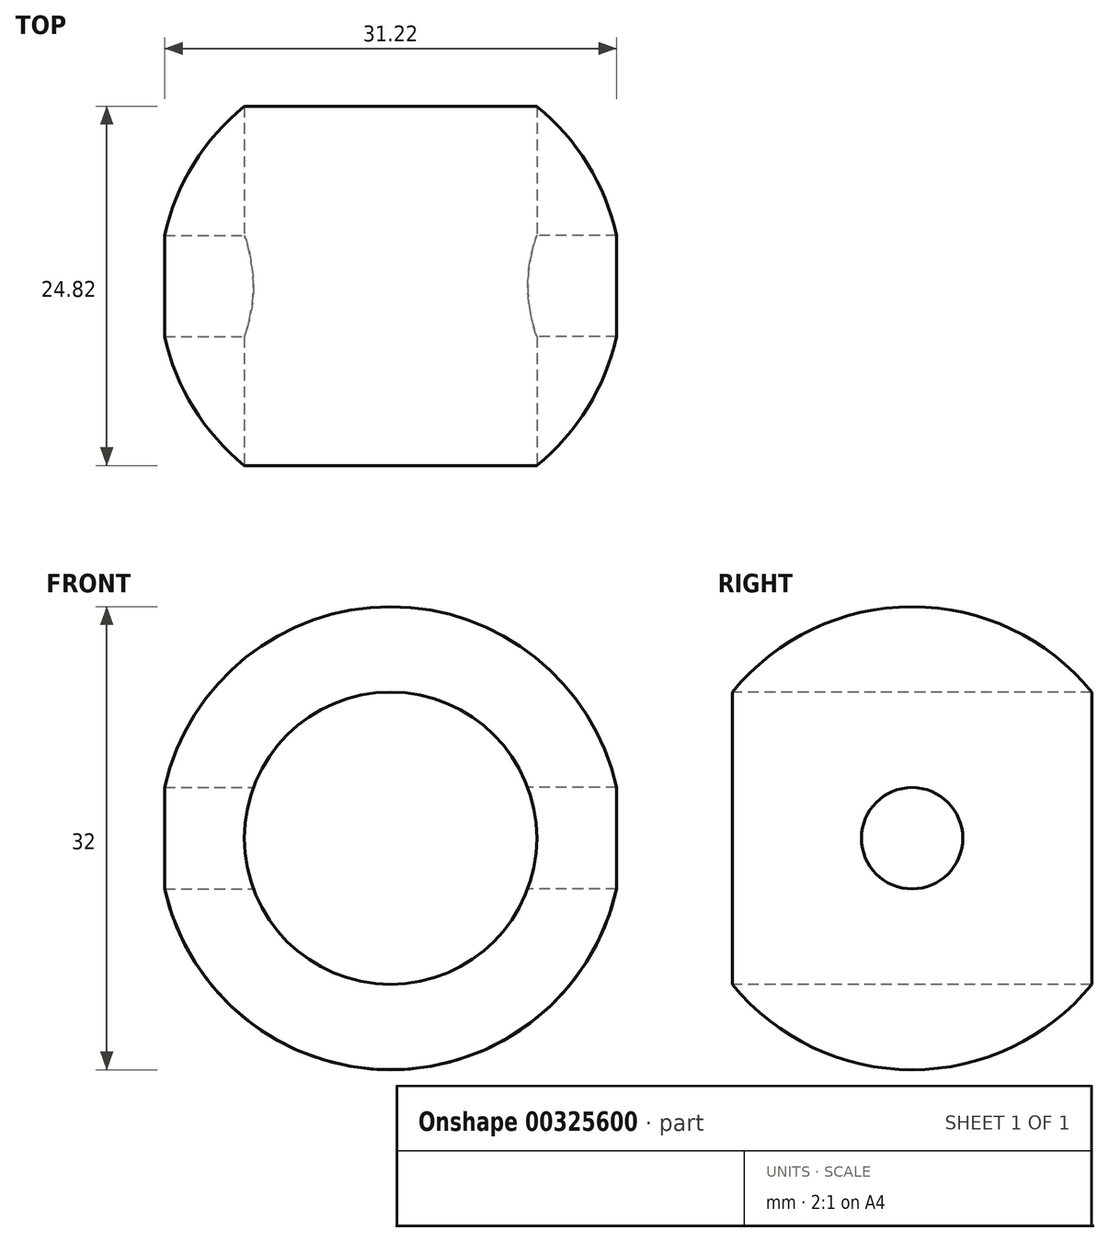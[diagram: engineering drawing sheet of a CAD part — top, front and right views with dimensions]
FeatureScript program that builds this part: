
annotation { "Feature Type Name" : "Feature", "Feature Type Description" : "" }
export const myFeature = defineFeature(function(context is Context, id is Id, definition is map)
    precondition{}
    {
        {
            var Q0;
            Q0=qCreatedBy(makeId("Front.planeOp"),FACE);
            var sketch = newSketch(context, id + "F0", { "sketchPlane" : qUnion([Q0])});
            skArc(sketch, "E0", {"start": v(16, 0) * mm, "mid": v(0, 16) * mm, "end": v(-16, 0) * mm});
            skLineSegment(sketch, "E1", {"start": v(0, 0) * mm, "end": v(16, 0) * mm});
            skLineSegment(sketch, "E2", {"start": v(0, 0) * mm, "end": v(-16, 0) * mm});
            skLineSegment(sketch, "E3", {"start": v(0, 0) * mm, "end": v(-41.5, 0) * mm, "construction": true});
            skLineSegment(sketch, "E4", {"start": v(-41.5, 0) * mm, "end": v(0, 0) * mm, "construction": true});
            skLineSegment(sketch, "E5", {"start": v(0, 0) * mm, "end": v(35.48, 0) * mm, "construction": true});
            skSolve(sketch);
        }
        {
            var Q0;
            Q0=makeQuery(id+"F0.imprint","IMPRINT",FACE,{"disambiguationData":[TD([[makeQuery(id+"F0.imprint","IMPRINT",EDGE,{"derivedFrom":sQuery(id+"F0.wireOp",EDGE,"E0")}),1.0]])]});
            var Q1;
            Q1=sQuery(id+"F0.wireOp",EDGE,"E5");
            revolve(context, id + "F1", {"entities" : qUnion([Q0]), "axis" : qUnion([Q1]), "revolveType" : RevolveType.SYMMETRIC, "angle" : 360 * degree});
        }
        {
            var Q0;
            Q0=qCreatedBy(makeId("Front.planeOp"),FACE);
            var sketch = newSketch(context, id + "F2", { "sketchPlane" : qUnion([Q0])});
            skPoint(sketch, "E6", {"position": v(0, 0) * mm});
            skSolve(sketch);
        }
        {
            var Q0;
            Q0=sQuery(id+"F2.wireOp",VERTEX,"E6");
            var Q1;
            Q1=makeQuery(id+"F1.opRevolve","SWEPT_BODY",BODY,{"disambiguationData":[OSD([sQuery(id+"F0.wireOp",EDGE,"E0"),sQuery(id+"F0.wireOp",EDGE,"E1"),sQuery(id+"F0.wireOp",EDGE,"E2")])]});
            hole(context, id + "F3", {"style" : HoleStyle.C_BORE, "endStyle" : HoleEndStyle.THROUGH, "holeDiameter" : 20.2 * mm, "cBoreDiameter" : 20.2 * mm, "cBoreDepth" : 500 * mm, "tappedDepth" : 12 * mm, "tapClearance" : 3, "locations" : qUnion([Q0]), "scope" : qUnion([Q1])});
        }
        {
            var Q0;
            Q0=qCreatedBy(makeId("Front.planeOp"),FACE);
            var sketch = newSketch(context, id + "F4", { "sketchPlane" : qUnion([Q0])});
            skPoint(sketch, "E7", {"position": v(0, 0) * mm});
            skSolve(sketch);
        }
        {
            var Q0;
            Q0=sQuery(id+"F4.wireOp",VERTEX,"E7");
            var Q1;
            Q1=makeQuery(id+"F1.opRevolve","SWEPT_BODY",BODY,{"disambiguationData":[OSD([sQuery(id+"F0.wireOp",EDGE,"E0"),sQuery(id+"F0.wireOp",EDGE,"E1"),sQuery(id+"F0.wireOp",EDGE,"E2")])]});
            hole(context, id + "F5", {"style" : HoleStyle.C_BORE, "endStyle" : HoleEndStyle.THROUGH, "oppositeDirection" : true, "holeDiameter" : 20.2 * mm, "cBoreDiameter" : 20.2 * mm, "cBoreDepth" : 500 * mm, "tappedDepth" : 12 * mm, "tapClearance" : 3, "locations" : qUnion([Q0]), "scope" : qUnion([Q1])});
        }
        {
            var Q0;
            Q0=qCreatedBy(makeId("Right.planeOp"),FACE);
            var sketch = newSketch(context, id + "F6", { "sketchPlane" : qUnion([Q0])});
            skPoint(sketch, "E8", {"position": v(0, 0) * mm});
            skSolve(sketch);
        }
        {
            var Q0;
            Q0=sQuery(id+"F6.wireOp",VERTEX,"E8");
            var Q1;
            Q1=makeQuery(id+"F1.opRevolve","SWEPT_BODY",BODY,{"disambiguationData":[OSD([sQuery(id+"F0.wireOp",EDGE,"E0"),sQuery(id+"F0.wireOp",EDGE,"E1"),sQuery(id+"F0.wireOp",EDGE,"E2")])]});
            hole(context, id + "F7", {"style" : HoleStyle.C_BORE, "endStyle" : HoleEndStyle.THROUGH, "oppositeDirection" : true, "holeDiameter" : 7 * mm, "cBoreDiameter" : 7 * mm, "cBoreDepth" : 500 * mm, "tappedDepth" : 12 * mm, "tapClearance" : 3, "startFromSketch" : true, "locations" : qUnion([Q0]), "scope" : qUnion([Q1])});
        }
        {
            var Q0;
            Q0=qCreatedBy(makeId("Right.planeOp"),FACE);
            var sketch = newSketch(context, id + "F8", { "sketchPlane" : qUnion([Q0])});
            skPoint(sketch, "E9", {"position": v(0, 0) * mm});
            skSolve(sketch);
        }
        {
            var Q0;
            Q0=sQuery(id+"F8.wireOp",VERTEX,"E9");
            var Q1;
            Q1=makeQuery(id+"F1.opRevolve","SWEPT_BODY",BODY,{"disambiguationData":[OSD([sQuery(id+"F0.wireOp",EDGE,"E0"),sQuery(id+"F0.wireOp",EDGE,"E1"),sQuery(id+"F0.wireOp",EDGE,"E2")])]});
            hole(context, id + "F9", {"style" : HoleStyle.C_BORE, "endStyle" : HoleEndStyle.THROUGH, "holeDiameter" : 7 * mm, "cBoreDiameter" : 7 * mm, "cBoreDepth" : 500 * mm, "tappedDepth" : 12 * mm, "tapClearance" : 3, "locations" : qUnion([Q0]), "scope" : qUnion([Q1])});
        }
    });
